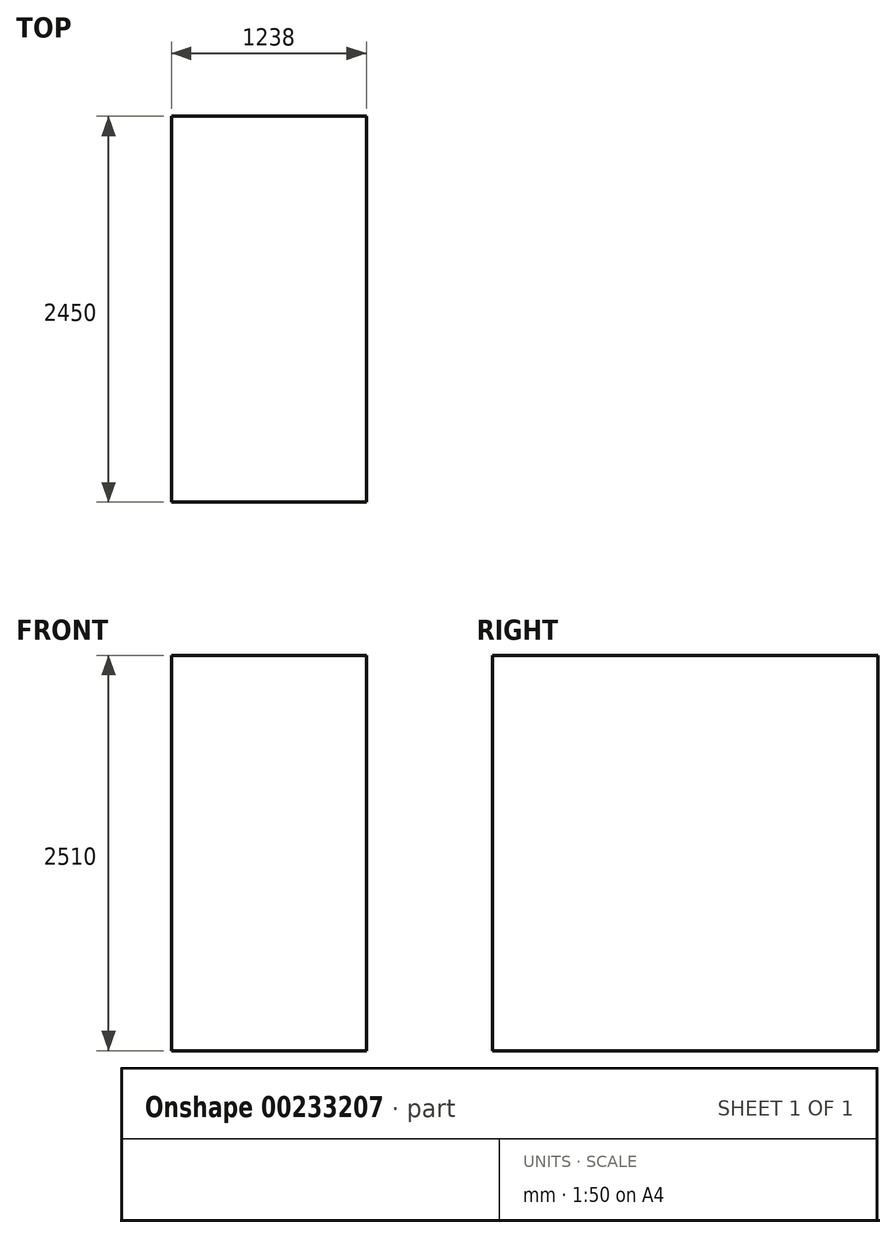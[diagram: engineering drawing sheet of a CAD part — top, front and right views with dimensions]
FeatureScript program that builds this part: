
annotation { "Feature Type Name" : "Feature", "Feature Type Description" : "" }
export const myFeature = defineFeature(function(context is Context, id is Id, definition is map)
    precondition{}
    {
        {
            var Q0;
            Q0=qCreatedBy(makeId("Top.planeOp"),FACE);
            var sketch = newSketch(context, id + "F0", { "sketchPlane" : qUnion([Q0])});
            skLineSegment(sketch, "E0.bottom", {"start": v(-629.38, 1377.31) * mm, "end": v(608.62, 1377.31) * mm});
            skLineSegment(sketch, "E0.top", {"start": v(-629.38, -1072.69) * mm, "end": v(608.62, -1072.69) * mm});
            skLineSegment(sketch, "E0.left", {"start": v(-629.38, 1377.31) * mm, "end": v(-629.38, -1072.69) * mm});
            skLineSegment(sketch, "E0.right", {"start": v(608.62, 1377.31) * mm, "end": v(608.62, -1072.69) * mm});
            skSolve(sketch);
        }
        {
            var Q0;
            Q0 = qSketchRegion(id + "F0", true);
            extrude(context, id + "F1", {"entities" : qUnion([Q0]), "depth" : 2510 * mm});
        }
    });
